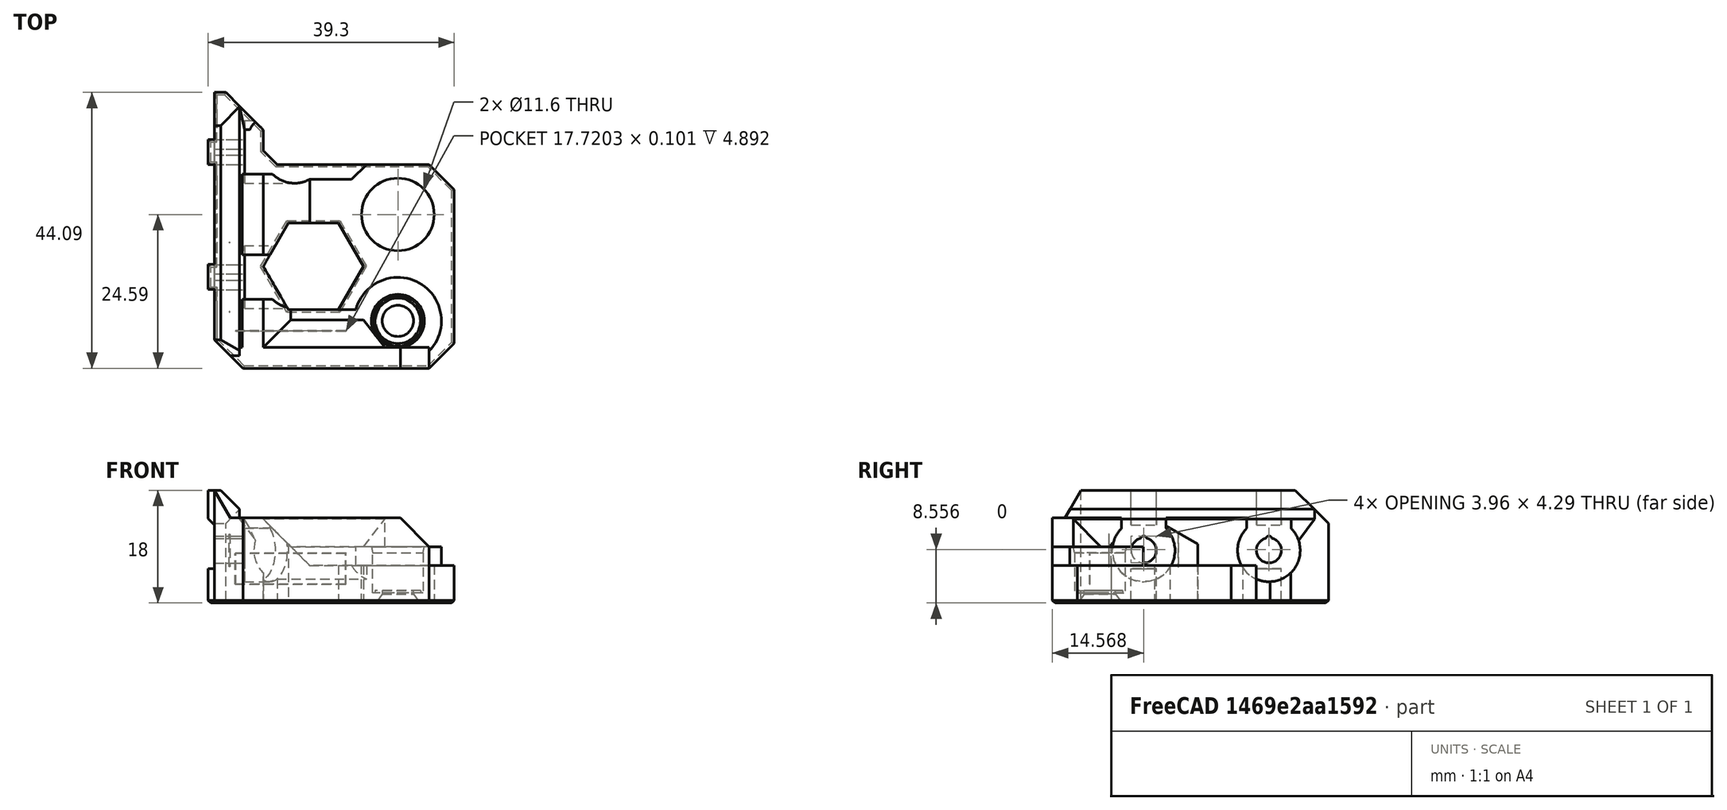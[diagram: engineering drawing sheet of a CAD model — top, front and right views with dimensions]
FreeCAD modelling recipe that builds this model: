
FCSTD DOCUMENT  (FreeCAD 0.18R14555 (Git shallow))
Label: Z-top
License: All rights reserved
LicenseURL: http://en.wikipedia.org/wiki/All_rights_reserved
objects: Part::Feature×7, Part::Cut×3, Part::MultiFuse×2, Part::Box×1, Part::Chamfer×1
note: 14 computed .brp shape members not serialized (recipe doc carries the construction recipe); baked Part::Feature solids carry a one-line shape summary decoded from their .brp

FEATURE [Part::Feature] Part__Feature  label="z_top v1"
  Placement = pos=(0,0,6) rot=(0,0,1;0rad)
  shape: bbox 39.72 x 44.11 x 18.02 mm, 127 faces (baked)
FEATURE [Part::Feature] Cut001  label="T-slot-align-chamfer-cut"
  Placement = pos=(-35.3,21.78,0) rot=(0,0,1;0rad)
  shape: bbox 5.4 x 10.45 x 30 mm, 15 faces (baked)
FEATURE [Part::Feature] Cut002  label="T-slot-align-chamfer-cut001"
  Placement = pos=(-35.3,1.78,0) rot=(0,0,1;0rad)
  shape: bbox 5.4 x 10.45 x 30 mm, 15 faces (baked)
FEATURE [Part::Feature] Part__Feature001  label="m5-to-m4-bolt-hole"
  Placement = pos=(-26.3,7,8.4) rot=(0,0,-1;1.5708rad)
  shape: bbox 3 x 6 x 6 mm, 5 faces (baked)
FEATURE [Part::Feature] Part__Feature002  label="m5-to-m4-bolt-hole001"
  Placement = pos=(-24.5,7,8.4) rot=(0,0,-1;1.5708rad)
  shape: bbox 3 x 6 x 6 mm, 5 faces (baked)
FEATURE [Part::MultiFuse] Fusion
  Shapes = -> [Part__Feature001,Part__Feature002]
FEATURE [Part::Feature] Fusion001
  Placement = pos=(0,20,0) rot=(0,0,1;0rad)
  shape: bbox 4.8 x 6 x 6 mm, 11 faces (baked)
FEATURE [Part::Box] Box  label="Cube"
  AttacherType = Attacher::AttachEngine3D
  Height = 8
  Length = 2
  Placement = pos=(-31.3,0,4.5) rot=(0,0,1;0rad)
  Width = 30
FEATURE [Part::Chamfer] Chamfer
  Base = -> Box
  Edges = 1 edges r=1: [Edge6]
  Placement = pos=(0,0,1) rot=(0,0,1;0rad)
FEATURE [Part::Cut] Cut
  Base = -> Part__Feature
  Tool = -> Cut001
FEATURE [Part::Cut] Cut003
  Base = -> Cut
  Tool = -> Cut002
FEATURE [Part::Cut] Cut004
  Base = -> Cut003
  Tool = -> Chamfer
FEATURE [Part::MultiFuse] Fusion002
  Shapes = -> [Cut004,Fusion,Fusion001]
FEATURE [Part::Feature] Fusion002001  label="Fusion003"
  shape: bbox 39.3 x 44.09 x 18 mm, 123 faces (baked)
